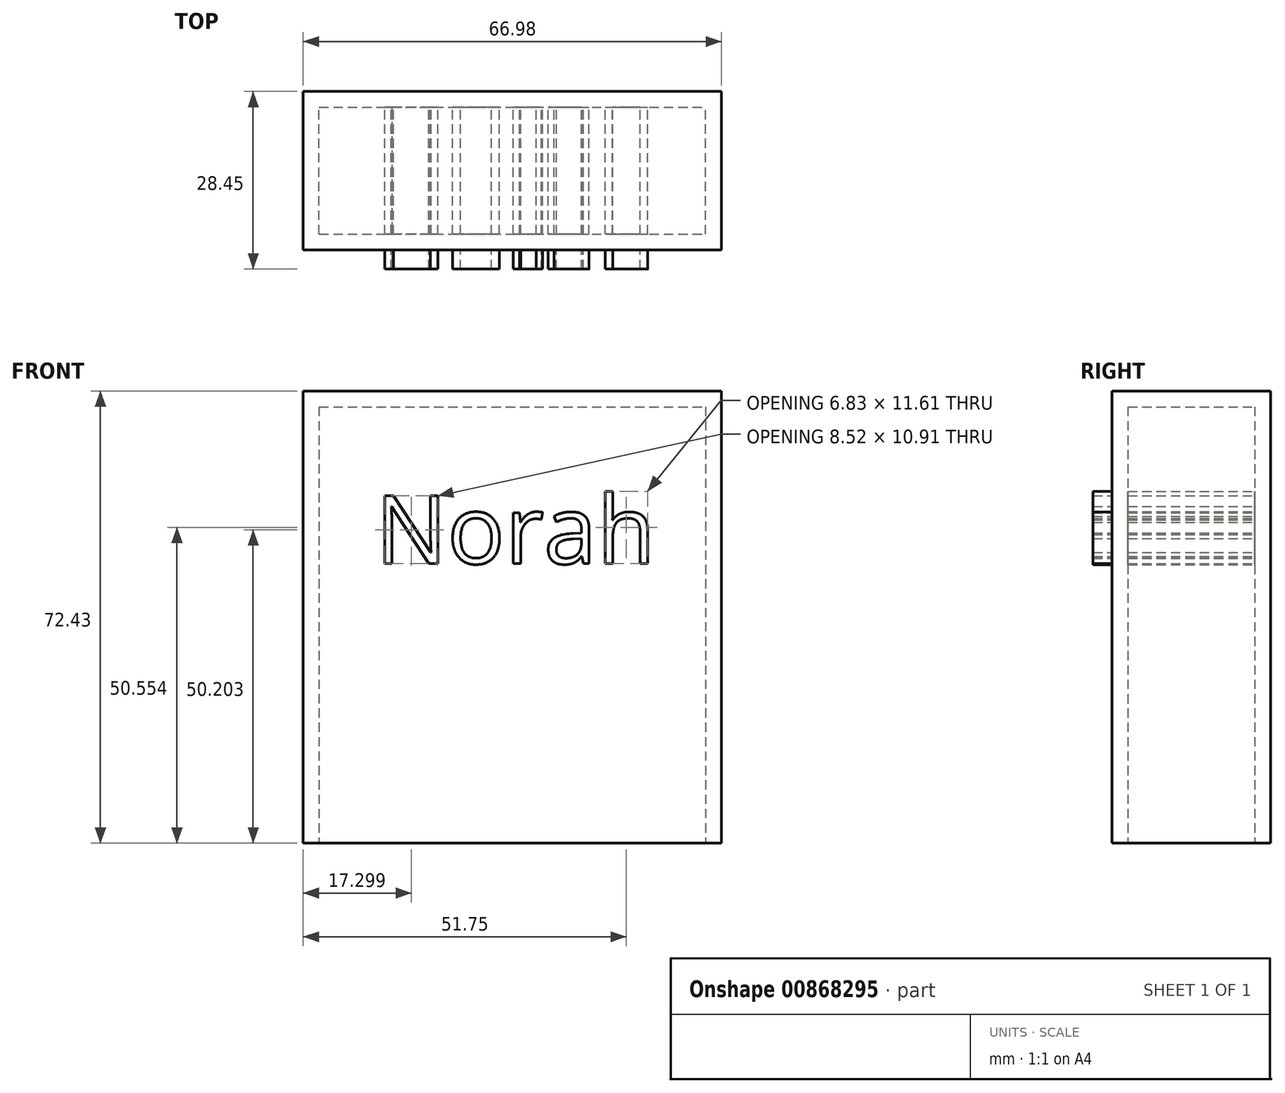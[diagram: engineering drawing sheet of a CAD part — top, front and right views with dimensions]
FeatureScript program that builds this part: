
annotation { "Feature Type Name" : "Feature", "Feature Type Description" : "" }
export const myFeature = defineFeature(function(context is Context, id is Id, definition is map)
    precondition{}
    {
        {
            var Q0;
            Q0=qCreatedBy(makeId("Front.planeOp"),FACE);
            var sketch = newSketch(context, id + "F0", { "sketchPlane" : qUnion([Q0])});
            skLineSegment(sketch, "E0.bottom", {"start": v(-33.06, 40.94) * mm, "end": v(33.92, 40.94) * mm});
            skLineSegment(sketch, "E0.top", {"start": v(-33.06, -31.49) * mm, "end": v(33.92, -31.49) * mm});
            skLineSegment(sketch, "E0.left", {"start": v(-33.06, 40.94) * mm, "end": v(-33.06, -31.49) * mm});
            skLineSegment(sketch, "E0.right", {"start": v(33.92, 40.94) * mm, "end": v(33.92, -31.49) * mm});
            skSolve(sketch);
        }
        {
            var Q0;
            Q0 = qSketchRegion(id + "F0", true);
            var Q1;
            Q1=makeQuery(id+"F0.imprint","IMPRINT",FACE,{"disambiguationData":[TD([[makeQuery(id+"F0.imprint","IMPRINT",EDGE,{"derivedFrom":sQuery(id+"F0.wireOp",EDGE,"E0.bottom")}),-1.0]])]});
            extrude(context, id + "F1", {"entities" : qUnion([Q0, Q1]), "depth" : 25.4 * mm, "offsetDistance" : 25.4 * mm});
        }
        {
            var Q0;
            Q0=makeQuery(id+"F1.opExtrude","SWEPT_FACE",FACE,{"disambiguationData":[OSD([sQuery(id+"F0.wireOp",EDGE,"E0.top")])]});
            shell(context, id + "F2", {"entities" : qUnion([Q0]), "thickness" : 2.54 * mm});
        }
        {
            var Q0;
            Q0=qCreatedBy(makeId("Front.planeOp"),FACE);
            var sketch = newSketch(context, id + "F3", { "sketchPlane" : qUnion([Q0])});
            skText(sketch, "E1", { "text": "Norah", "fontName": "OpenSans-Regular.ttf"});
            const initialGuessF3  = {"E1": [-0.02152, 0.01326, 1, 0, 0.011]};
            skSetInitialGuess(sketch, initialGuessF3);
            skSolve(sketch);
        }
        {
            var Q0;
            Q0 = qSketchRegion(id + "F3", true);
            extrude(context, id + "F4", {"entities" : qUnion([Q0]), "operationType" : NewBodyOperationType.ADD, "depth" : 28.45 * mm, "offsetDistance" : 25.4 * mm});
        }
    });
